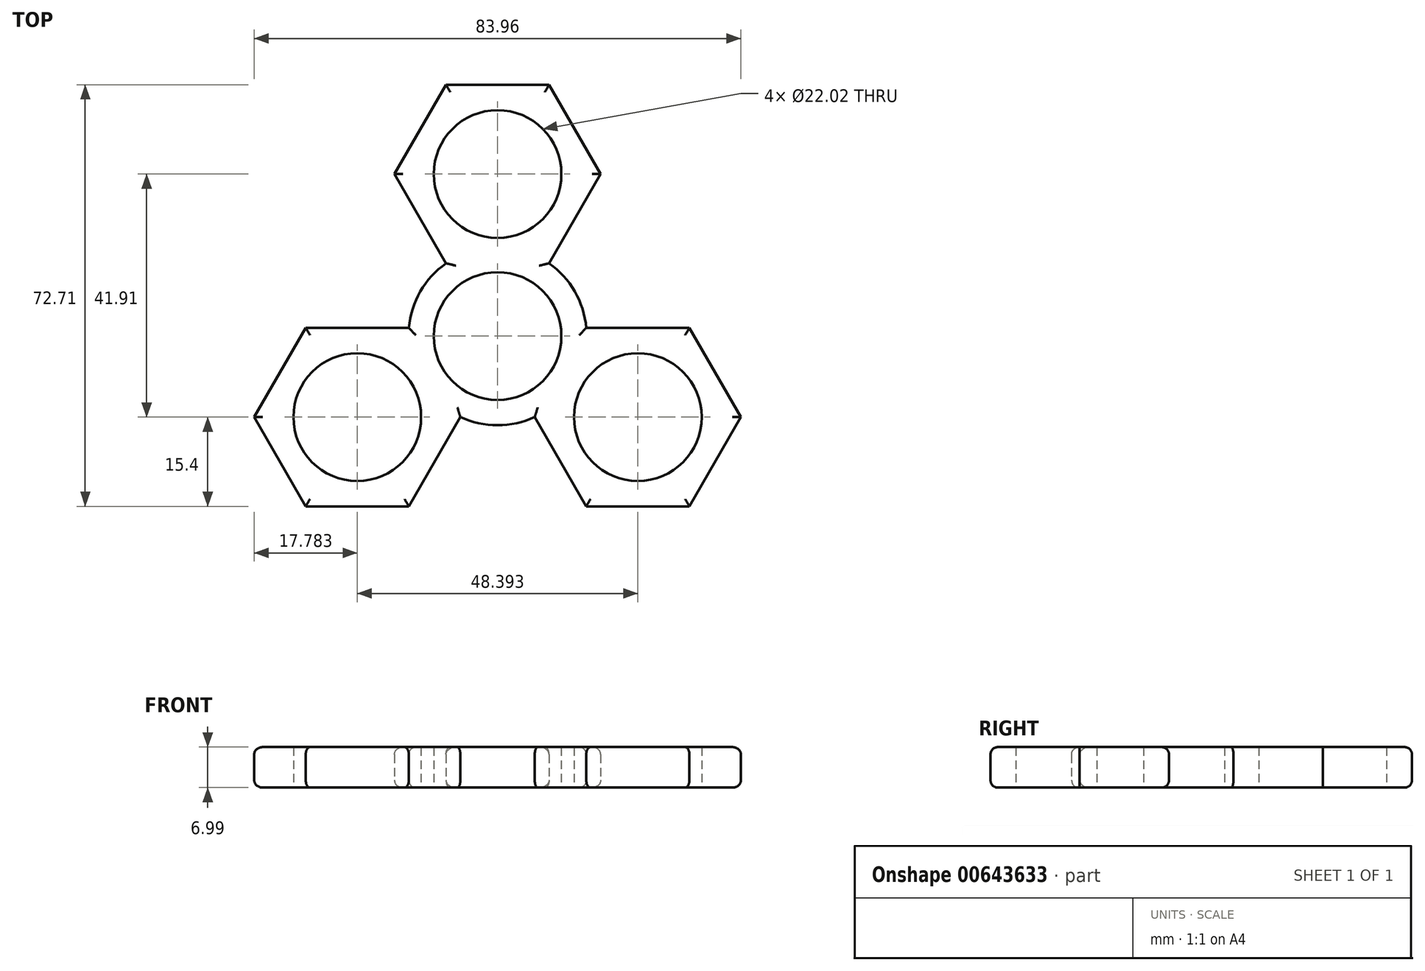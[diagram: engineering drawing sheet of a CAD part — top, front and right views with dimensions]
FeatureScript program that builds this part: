
annotation { "Feature Type Name" : "Feature", "Feature Type Description" : "" }
export const myFeature = defineFeature(function(context is Context, id is Id, definition is map)
    precondition{}
    {
        {
            var Q0;
            Q0=qCreatedBy(makeId("Top.planeOp"),FACE);
            var sketch = newSketch(context, id + "F0", { "sketchPlane" : qUnion([Q0])});
            skCircle(sketch, "E0", {"center": v(0, 0) * mm, "radius": 11.01 * mm});
            skCircle(sketch, "E1", {"center": v(-24.2, -13.97) * mm, "radius": 11.01 * mm});
            skCircle(sketch, "E2", {"center": v(24.2, -13.97) * mm, "radius": 11.01 * mm});
            skCircle(sketch, "E3", {"center": v(0, 27.94) * mm, "radius": 11.01 * mm});
            skLineSegment(sketch, "E4", {"start": v(0, 0) * mm, "end": v(0, 27.94) * mm});
            skLineSegment(sketch, "E5", {"start": v(0, 0) * mm, "end": v(-24.2, -13.97) * mm});
            skLineSegment(sketch, "E6", {"start": v(0, 0) * mm, "end": v(24.2, -13.97) * mm});
            skCircle(sketch, "E7.cCircle", {"center": v(0, 27.94) * mm, "radius": 17.78 * mm, "construction": true});
            skLineSegment(sketch, "E7.0", {"start": v(8.9, 12.54) * mm, "end": v(-8.89, 12.54) * mm});
            skLineSegment(sketch, "E7.1", {"start": v(-8.89, 12.54) * mm, "end": v(-17.78, 27.94) * mm});
            skLineSegment(sketch, "E7.2", {"start": v(-17.78, 27.94) * mm, "end": v(-8.9, 43.34) * mm});
            skLineSegment(sketch, "E7.3", {"start": v(-8.9, 43.34) * mm, "end": v(8.89, 43.34) * mm});
            skLineSegment(sketch, "E7.4", {"start": v(8.89, 43.34) * mm, "end": v(17.78, 27.94) * mm});
            skLineSegment(sketch, "E7.5", {"start": v(17.78, 27.94) * mm, "end": v(8.9, 12.54) * mm});
            skCircle(sketch, "E8.cCircle", {"center": v(-24.2, -13.97) * mm, "radius": 17.78 * mm, "construction": true});
            skLineSegment(sketch, "E8.0", {"start": v(-15.3, -29.37) * mm, "end": v(-33.09, -29.37) * mm});
            skLineSegment(sketch, "E8.1", {"start": v(-33.09, -29.37) * mm, "end": v(-41.98, -13.97) * mm});
            skLineSegment(sketch, "E8.2", {"start": v(-41.98, -13.97) * mm, "end": v(-33.09, 1.43) * mm});
            skLineSegment(sketch, "E8.3", {"start": v(-33.09, 1.43) * mm, "end": v(-15.3, 1.43) * mm});
            skLineSegment(sketch, "E8.4", {"start": v(-15.3, 1.43) * mm, "end": v(-6.42, -13.97) * mm});
            skLineSegment(sketch, "E8.5", {"start": v(-6.42, -13.97) * mm, "end": v(-15.3, -29.37) * mm});
            skCircle(sketch, "E9.cCircle", {"center": v(24.2, -13.97) * mm, "radius": 17.78 * mm, "construction": true});
            skLineSegment(sketch, "E9.0", {"start": v(15.3, -29.37) * mm, "end": v(6.42, -13.97) * mm});
            skLineSegment(sketch, "E9.1", {"start": v(6.42, -13.97) * mm, "end": v(15.3, 1.43) * mm});
            skLineSegment(sketch, "E9.2", {"start": v(15.3, 1.43) * mm, "end": v(33.09, 1.43) * mm});
            skLineSegment(sketch, "E9.3", {"start": v(33.09, 1.43) * mm, "end": v(41.98, -13.97) * mm});
            skLineSegment(sketch, "E9.4", {"start": v(41.98, -13.97) * mm, "end": v(33.09, -29.37) * mm});
            skLineSegment(sketch, "E9.5", {"start": v(33.09, -29.37) * mm, "end": v(15.3, -29.37) * mm});
            skCircle(sketch, "E10", {"center": v(0, 0) * mm, "radius": 15.37 * mm});
            skSolve(sketch);
        }
        {
            var Q0;
            Q0 = qSketchRegion(id + "F0", true);
            extrude(context, id + "F1", {"entities" : qUnion([Q0]), "depth" : 7 * mm, "offsetDistance" : 25.4 * mm});
        }
        {
            var Q0;
            Q0=makeQuery(id+"F1.opExtrude","CAP_EDGE",EDGE,{"disambiguationData":[OSD([sQuery(id+"F0.wireOp",EDGE,"E7.1")])],"isStart":false});
            var Q1;
            Q1=makeQuery(id+"F1.opExtrude","CAP_EDGE",EDGE,{"disambiguationData":[OSD([sQuery(id+"F0.wireOp",EDGE,"E7.2")])],"isStart":false});
            var Q2;
            Q2=makeQuery(id+"F1.opExtrude","CAP_EDGE",EDGE,{"disambiguationData":[OSD([sQuery(id+"F0.wireOp",EDGE,"E7.3")])],"isStart":false});
            var Q3;
            Q3=makeQuery(id+"F1.opExtrude","CAP_EDGE",EDGE,{"disambiguationData":[OSD([sQuery(id+"F0.wireOp",EDGE,"E7.4")])],"isStart":false});
            var Q4;
            Q4=makeQuery(id+"F1.opExtrude","CAP_EDGE",EDGE,{"disambiguationData":[OSD([sQuery(id+"F0.wireOp",EDGE,"E7.5")])],"isStart":false});
            var Q5;
            {var subQ0=sQuery(id+"F0.wireOp",EDGE,"E10");Q5=makeQuery(id+"F1.opExtrude","CAP_EDGE",EDGE,{"disambiguationData":[OSD([subQ0]),TDD([makeQuery(id+"F0.imprint","IMPRINT",EDGE,{"disambiguationData":[TD([[makeQuery(id+"F0.imprint","INTERSECT",VERTEX,{"derivedFrom":[sQuery(id+"F0.wireOp",EDGE,"E7.0"),sQuery(id+"F0.wireOp",EDGE,"E7.5"),subQ0]}),1.0]])],"derivedFrom":subQ0})])],"isStart":false});}
            var Q6;
            {var subQ0=sQuery(id+"F0.wireOp",EDGE,"E10");Q6=makeQuery(id+"F1.opExtrude","CAP_EDGE",EDGE,{"disambiguationData":[OSD([subQ0]),TDD([makeQuery(id+"F0.imprint","IMPRINT",EDGE,{"disambiguationData":[TD([[makeQuery(id+"F0.imprint","INTERSECT",VERTEX,{"derivedFrom":[sQuery(id+"F0.wireOp",EDGE,"E7.0"),sQuery(id+"F0.wireOp",EDGE,"E7.1"),subQ0]}),-1.0]])],"derivedFrom":subQ0})])],"isStart":false});}
            var Q7;
            Q7=makeQuery(id+"F1.opExtrude","CAP_EDGE",EDGE,{"disambiguationData":[OSD([sQuery(id+"F0.wireOp",EDGE,"E8.3")])],"isStart":false});
            var Q8;
            Q8=makeQuery(id+"F1.opExtrude","CAP_EDGE",EDGE,{"disambiguationData":[OSD([sQuery(id+"F0.wireOp",EDGE,"E8.2")])],"isStart":false});
            var Q9;
            Q9=makeQuery(id+"F1.opExtrude","CAP_EDGE",EDGE,{"disambiguationData":[OSD([sQuery(id+"F0.wireOp",EDGE,"E8.1")])],"isStart":false});
            var Q10;
            Q10=makeQuery(id+"F1.opExtrude","CAP_EDGE",EDGE,{"disambiguationData":[OSD([sQuery(id+"F0.wireOp",EDGE,"E8.0")])],"isStart":false});
            var Q11;
            {var subQ0=sQuery(id+"F0.wireOp",EDGE,"E10");Q11=makeQuery(id+"F1.opExtrude","CAP_EDGE",EDGE,{"disambiguationData":[OSD([subQ0]),TDD([makeQuery(id+"F0.imprint","IMPRINT",EDGE,{"disambiguationData":[TD([[makeQuery(id+"F0.imprint","INTERSECT",VERTEX,{"derivedFrom":[sQuery(id+"F0.wireOp",EDGE,"E8.4"),sQuery(id+"F0.wireOp",EDGE,"E8.5"),subQ0]}),-1.0]])],"derivedFrom":subQ0})])],"isStart":false});}
            var Q12;
            Q12=makeQuery(id+"F1.opExtrude","CAP_EDGE",EDGE,{"disambiguationData":[OSD([sQuery(id+"F0.wireOp",EDGE,"E9.0")])],"isStart":false});
            var Q13;
            Q13=makeQuery(id+"F1.opExtrude","CAP_EDGE",EDGE,{"disambiguationData":[OSD([sQuery(id+"F0.wireOp",EDGE,"E9.5")])],"isStart":false});
            var Q14;
            Q14=makeQuery(id+"F1.opExtrude","CAP_EDGE",EDGE,{"disambiguationData":[OSD([sQuery(id+"F0.wireOp",EDGE,"E9.4")])],"isStart":false});
            var Q15;
            Q15=makeQuery(id+"F1.opExtrude","CAP_EDGE",EDGE,{"disambiguationData":[OSD([sQuery(id+"F0.wireOp",EDGE,"E9.3")])],"isStart":false});
            var Q16;
            Q16=makeQuery(id+"F1.opExtrude","CAP_EDGE",EDGE,{"disambiguationData":[OSD([sQuery(id+"F0.wireOp",EDGE,"E9.2")])],"isStart":false});
            var Q17;
            Q17=makeQuery(id+"F1.opExtrude","CAP_EDGE",EDGE,{"disambiguationData":[OSD([sQuery(id+"F0.wireOp",EDGE,"E8.5")])],"isStart":false});
            fillet(context, id + "F2", {"entities" : qUnion([Q0, Q1, Q2, Q3, Q4, Q5, Q6, Q7, Q8, Q9, Q10, Q11, Q12, Q13, Q14, Q15, Q16, Q17]), "radius" : 1.27 * mm, "tangentPropagation" : true, "allowEdgeOverflow" : false});
        }
        {
            var Q0;
            Q0=makeQuery(id+"F1.opExtrude","CAP_EDGE",EDGE,{"disambiguationData":[OSD([sQuery(id+"F0.wireOp",EDGE,"E8.0")])],"isStart":true});
            var Q1;
            Q1=makeQuery(id+"F1.opExtrude","CAP_EDGE",EDGE,{"disambiguationData":[OSD([sQuery(id+"F0.wireOp",EDGE,"E8.5")])],"isStart":true});
            var Q2;
            Q2=makeQuery(id+"F1.opExtrude","CAP_EDGE",EDGE,{"disambiguationData":[OSD([sQuery(id+"F0.wireOp",EDGE,"E8.1")])],"isStart":true});
            var Q3;
            Q3=makeQuery(id+"F1.opExtrude","CAP_EDGE",EDGE,{"disambiguationData":[OSD([sQuery(id+"F0.wireOp",EDGE,"E8.2")])],"isStart":true});
            var Q4;
            Q4=makeQuery(id+"F1.opExtrude","CAP_EDGE",EDGE,{"disambiguationData":[OSD([sQuery(id+"F0.wireOp",EDGE,"E8.3")])],"isStart":true});
            var Q5;
            {var subQ0=sQuery(id+"F0.wireOp",EDGE,"E10");Q5=makeQuery(id+"F1.opExtrude","CAP_EDGE",EDGE,{"disambiguationData":[OSD([subQ0]),TDD([makeQuery(id+"F0.imprint","IMPRINT",EDGE,{"disambiguationData":[TD([[makeQuery(id+"F0.imprint","INTERSECT",VERTEX,{"derivedFrom":[sQuery(id+"F0.wireOp",EDGE,"E7.0"),sQuery(id+"F0.wireOp",EDGE,"E7.1"),subQ0]}),-1.0]])],"derivedFrom":subQ0})])],"isStart":true});}
            var Q6;
            Q6=makeQuery(id+"F1.opExtrude","CAP_EDGE",EDGE,{"disambiguationData":[OSD([sQuery(id+"F0.wireOp",EDGE,"E7.1")])],"isStart":true});
            var Q7;
            Q7=makeQuery(id+"F1.opExtrude","CAP_EDGE",EDGE,{"disambiguationData":[OSD([sQuery(id+"F0.wireOp",EDGE,"E7.2")])],"isStart":true});
            var Q8;
            Q8=makeQuery(id+"F1.opExtrude","CAP_EDGE",EDGE,{"disambiguationData":[OSD([sQuery(id+"F0.wireOp",EDGE,"E7.3")])],"isStart":true});
            var Q9;
            Q9=makeQuery(id+"F1.opExtrude","CAP_EDGE",EDGE,{"disambiguationData":[OSD([sQuery(id+"F0.wireOp",EDGE,"E7.4")])],"isStart":true});
            var Q10;
            Q10=makeQuery(id+"F1.opExtrude","CAP_EDGE",EDGE,{"disambiguationData":[OSD([sQuery(id+"F0.wireOp",EDGE,"E7.5")])],"isStart":true});
            var Q11;
            {var subQ0=sQuery(id+"F0.wireOp",EDGE,"E10");Q11=makeQuery(id+"F1.opExtrude","CAP_EDGE",EDGE,{"disambiguationData":[OSD([subQ0]),TDD([makeQuery(id+"F0.imprint","IMPRINT",EDGE,{"disambiguationData":[TD([[makeQuery(id+"F0.imprint","INTERSECT",VERTEX,{"derivedFrom":[sQuery(id+"F0.wireOp",EDGE,"E7.0"),sQuery(id+"F0.wireOp",EDGE,"E7.5"),subQ0]}),1.0]])],"derivedFrom":subQ0})])],"isStart":true});}
            var Q12;
            Q12=makeQuery(id+"F1.opExtrude","CAP_EDGE",EDGE,{"disambiguationData":[OSD([sQuery(id+"F0.wireOp",EDGE,"E9.2")])],"isStart":true});
            var Q13;
            Q13=makeQuery(id+"F1.opExtrude","CAP_EDGE",EDGE,{"disambiguationData":[OSD([sQuery(id+"F0.wireOp",EDGE,"E9.3")])],"isStart":true});
            var Q14;
            Q14=makeQuery(id+"F1.opExtrude","CAP_EDGE",EDGE,{"disambiguationData":[OSD([sQuery(id+"F0.wireOp",EDGE,"E9.4")])],"isStart":true});
            var Q15;
            Q15=makeQuery(id+"F1.opExtrude","CAP_EDGE",EDGE,{"disambiguationData":[OSD([sQuery(id+"F0.wireOp",EDGE,"E9.5")])],"isStart":true});
            var Q16;
            Q16=makeQuery(id+"F1.opExtrude","CAP_EDGE",EDGE,{"disambiguationData":[OSD([sQuery(id+"F0.wireOp",EDGE,"E9.0")])],"isStart":true});
            var Q17;
            {var subQ0=sQuery(id+"F0.wireOp",EDGE,"E10");Q17=makeQuery(id+"F1.opExtrude","CAP_EDGE",EDGE,{"disambiguationData":[OSD([subQ0]),TDD([makeQuery(id+"F0.imprint","IMPRINT",EDGE,{"disambiguationData":[TD([[makeQuery(id+"F0.imprint","INTERSECT",VERTEX,{"derivedFrom":[sQuery(id+"F0.wireOp",EDGE,"E8.4"),sQuery(id+"F0.wireOp",EDGE,"E8.5"),subQ0]}),-1.0]])],"derivedFrom":subQ0})])],"isStart":true});}
            fillet(context, id + "F3", {"entities" : qUnion([Q0, Q1, Q2, Q3, Q4, Q5, Q6, Q7, Q8, Q9, Q10, Q11, Q12, Q13, Q14, Q15, Q16, Q17]), "radius" : 1.27 * mm, "tangentPropagation" : true, "allowEdgeOverflow" : false});
        }
    });
